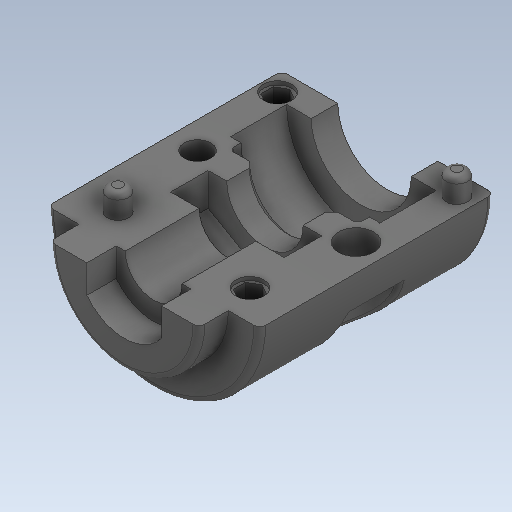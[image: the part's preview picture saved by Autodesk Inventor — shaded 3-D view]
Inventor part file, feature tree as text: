
AUTODESK INVENTOR PART (.ipt)
format: ipt  version: 2020 (Build 240168000, 168)  size: 268,800 bytes
history: native  units: in
note: dims shown in document units (in); Inventor stores cm internally (conversion verified against a paired STEP export)
features: fillet x1
ambient origin geometry x8: Origin, YZ Plane, XZ Plane, XY Plane, X Axis, Y Axis, Z Axis, Center Point
bodies: Solid1 (feature_tree)
feature tree (1):
  fillet  "Fillet1"  [1 undecoded]
note: 1 required parameter value undecoded (feature->parameter linkage not recoverable at this tier; creation-order binding heuristic only, values carry confidence <= 0.55)
